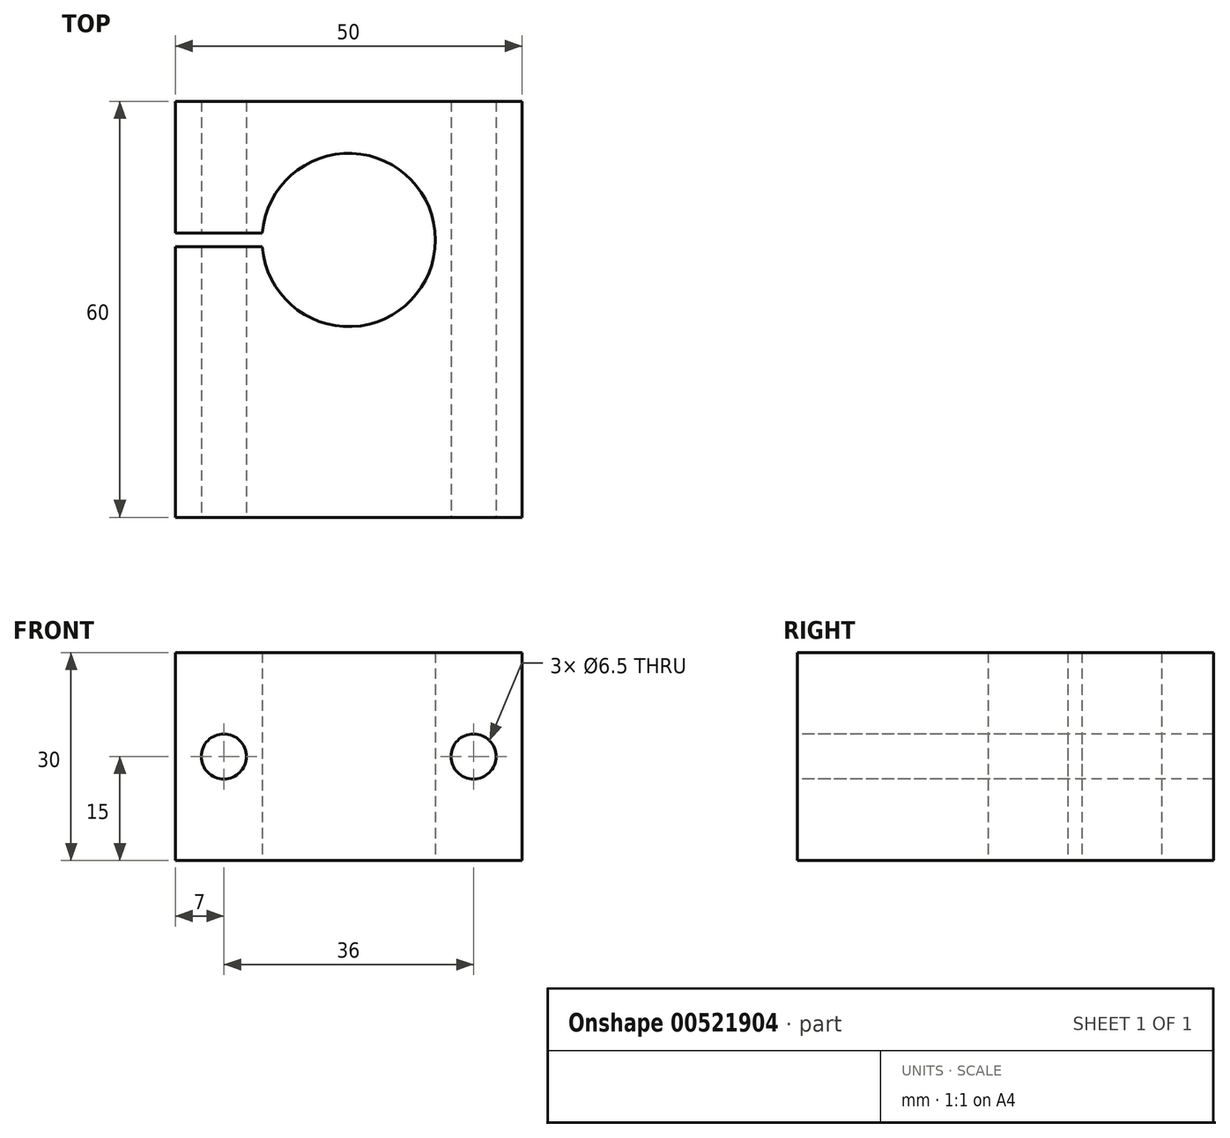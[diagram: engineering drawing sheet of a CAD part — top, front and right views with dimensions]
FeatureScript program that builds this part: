
annotation { "Feature Type Name" : "Feature", "Feature Type Description" : "" }
export const myFeature = defineFeature(function(context is Context, id is Id, definition is map)
    precondition{}
    {
        {
            var Q0;
            Q0=qCreatedBy(makeId("Top.planeOp"),FACE);
            var sketch = newSketch(context, id + "F0", { "sketchPlane" : qUnion([Q0])});
            skLineSegment(sketch, "E0.bottom", {"start": v(-25, -40) * mm, "end": v(25, -40) * mm});
            skLineSegment(sketch, "E0.top", {"start": v(-25, 20) * mm, "end": v(25, 20) * mm});
            skLineSegment(sketch, "E0.right", {"start": v(25, -40) * mm, "end": v(25, 20) * mm});
            skArc(sketch, "E1", {"start": v(-12.46, -1) * mm, "mid": v(1.28, -12.43) * mm, "end": v(12.4, 1.56) * mm});
            skLineSegment(sketch, "E2", {"start": v(-25, 20) * mm, "end": v(-25, 1) * mm});
            skLineSegment(sketch, "E3", {"start": v(-25, -40) * mm, "end": v(-25, -1) * mm});
            skLineSegment(sketch, "E4", {"start": v(-25, 1) * mm, "end": v(-12.46, 1) * mm});
            skLineSegment(sketch, "E5", {"start": v(-25, -1) * mm, "end": v(-12.46, -1) * mm});
            skArc(sketch, "E6.trimOffspring", {"start": v(12.4, 1.56) * mm, "mid": v(-0.28, 12.5) * mm, "end": v(-12.46, 1) * mm});
            skSolve(sketch);
        }
        {
            var Q0;
            Q0=qSketchRegion(id+"F0",true);
            extrude(context, id + "F1", {"entities" : qUnion([Q0]), "depth" : 30 * mm, "offsetDistance" : 25 * mm});
        }
        {
            var Q0;
            Q0=makeQuery(id+"F1.opExtrude","SWEPT_FACE",FACE,{"disambiguationData":[OSD([sQuery(id+"F0.wireOp",EDGE,"E0.bottom")])]});
            var sketch = newSketch(context, id + "F2", { "sketchPlane" : qUnion([Q0])});
            skCircle(sketch, "E7", {"center": v(-18, 15) * mm, "radius": 3.25 * mm});
            skPoint(sketch, "E7.centerSnap0", {"position": v(-25, 15) * mm});
            skCircle(sketch, "E8", {"center": v(18, 15) * mm, "radius": 3.25 * mm});
            skPoint(sketch, "E8.centerSnap0", {"position": v(25, 15) * mm});
            skSolve(sketch);
        }
        {
            var Q0;
            Q0=qSketchRegion(id+"F2",true);
            extrude(context, id + "F3", {"entities" : qUnion([Q0]), "operationType" : NewBodyOperationType.REMOVE, "endBound" : BoundingType.THROUGH_ALL, "oppositeDirection" : true, "depth" : 25 * mm, "offsetDistance" : 25 * mm});
        }
    });
